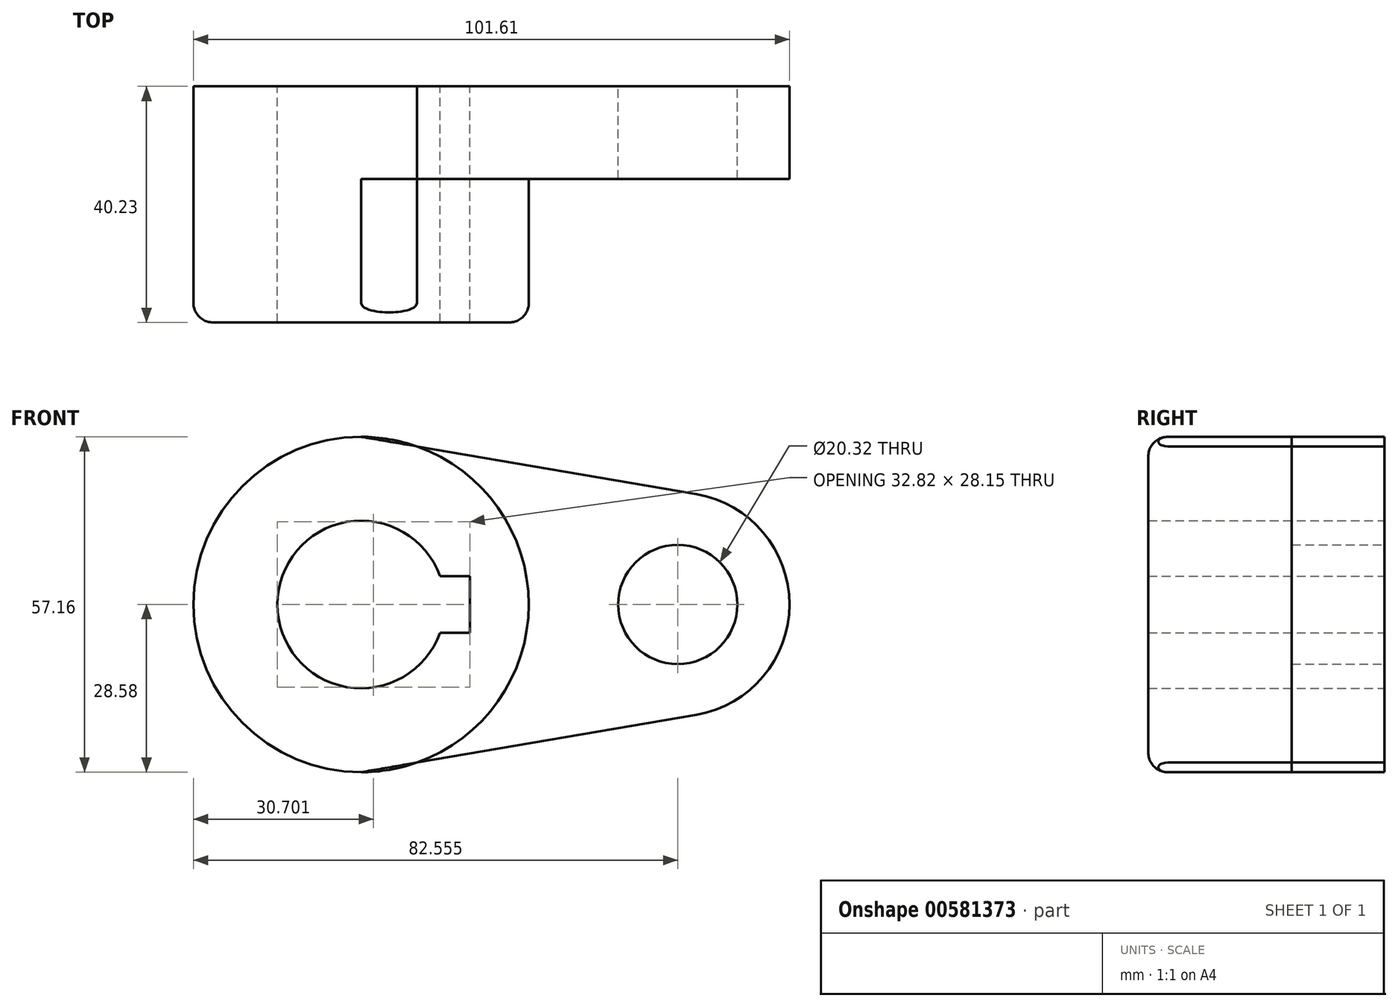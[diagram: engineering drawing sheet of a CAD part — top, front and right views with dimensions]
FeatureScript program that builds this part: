
annotation { "Feature Type Name" : "Feature", "Feature Type Description" : "" }
export const myFeature = defineFeature(function(context is Context, id is Id, definition is map)
    precondition{}
    {
        {
            var Q0;
            Q0=qCreatedBy(makeId("Front.planeOp"),FACE);
            var sketch = newSketch(context, id + "F0", { "sketchPlane" : qUnion([Q0])});
            skCircle(sketch, "E0", {"center": v(0, 0) * mm, "radius": 28.58 * mm});
            skCircle(sketch, "E1", {"center": v(53.98, 0) * mm, "radius": 19.05 * mm});
            skLineSegment(sketch, "E2", {"start": v(0, 28.58) * mm, "end": v(57.2, 18.78) * mm});
            skLineSegment(sketch, "E3", {"start": v(0, -28.58) * mm, "end": v(57.2, -18.78) * mm});
            skCircle(sketch, "E4", {"center": v(0, 0) * mm, "radius": 14.29 * mm});
            skCircle(sketch, "E5", {"center": v(53.98, 0) * mm, "radius": 10.16 * mm});
            skLineSegment(sketch, "E6.bottom", {"start": v(18.53, 4.83) * mm, "end": v(-18.53, 4.83) * mm});
            skLineSegment(sketch, "E6.top", {"start": v(18.53, -4.83) * mm, "end": v(-18.53, -4.83) * mm});
            skLineSegment(sketch, "E6.left", {"start": v(18.53, 4.83) * mm, "end": v(18.53, -4.83) * mm});
            skLineSegment(sketch, "E6.right", {"start": v(-18.53, 4.83) * mm, "end": v(-18.53, -4.83) * mm});
            skPoint(sketch, "E7", {"position": v(-14.29, 0) * mm});
            skSolve(sketch);
        }
        {
            var Q0;
            {var subQ0=sQuery(id+"F0.wireOp",EDGE,"E2");var subQ1=sQuery(id+"F0.wireOp",EDGE,"E0");var subQ2=makeQuery(id+"F0.imprint","INTERSECT",VERTEX,{"disambiguationData":[OD(0.0)],"derivedFrom":[subQ1,subQ0]});Q0=makeQuery(id+"F0.imprint","IMPRINT",FACE,{"disambiguationData":[TD([[makeQuery(id+"F0.imprint","IMPRINT",EDGE,{"disambiguationData":[TD([[subQ2,1.0]])],"derivedFrom":subQ1}),1.0]])]});}
            var Q1;
            {var subQ0=sQuery(id+"F0.wireOp",EDGE,"E3");var subQ1=sQuery(id+"F0.wireOp",EDGE,"E0");var subQ2=makeQuery(id+"F0.imprint","INTERSECT",VERTEX,{"disambiguationData":[OD(0.0)],"derivedFrom":[subQ1,subQ0]});Q1=makeQuery(id+"F0.imprint","IMPRINT",FACE,{"disambiguationData":[TD([[makeQuery(id+"F0.imprint","IMPRINT",EDGE,{"disambiguationData":[TD([[subQ2,-1.0]])],"derivedFrom":subQ1}),1.0]])]});}
            var Q2;
            {var subQ4=sQuery(id+"F0.wireOp",EDGE,"E6.left");Q2=makeQuery(id+"F0.imprint","IMPRINT",FACE,{"disambiguationData":[TD([[makeQuery(id+"F0.imprint","IMPRINT",EDGE,{"derivedFrom":subQ4}),1.0]])]});}
            var Q3;
            {var subQ5=sQuery(id+"F0.wireOp",EDGE,"E6.right");Q3=makeQuery(id+"F0.imprint","IMPRINT",FACE,{"disambiguationData":[TD([[makeQuery(id+"F0.imprint","IMPRINT",EDGE,{"derivedFrom":subQ5}),1.0]])]});}
            extrude(context, id + "F1", {"entities" : qUnion([Q0, Q1, Q2, Q3]), "depth" : 40.23 * mm, "offsetDistance" : 25.4 * mm});
        }
        {
            var Q0;
            Q0 = qSketchRegion(id + "F0", true);
            extrude(context, id + "F2", {"entities" : qUnion([Q0]), "operationType" : NewBodyOperationType.ADD, "depth" : 15.77 * mm, "offsetDistance" : 25.4 * mm});
        }
        {
            var Q0;
            Q0=makeQuery(id+"F1.opExtrude","CAP_EDGE",EDGE,{"disambiguationData":[OSD([sQuery(id+"F0.wireOp",EDGE,"E0")])],"isStart":false});
            fillet(context, id + "F3", {"entities" : qUnion([Q0]), "radius" : 3.3 * mm, "tangentPropagation" : true, "allowEdgeOverflow" : false});
        }
    });
